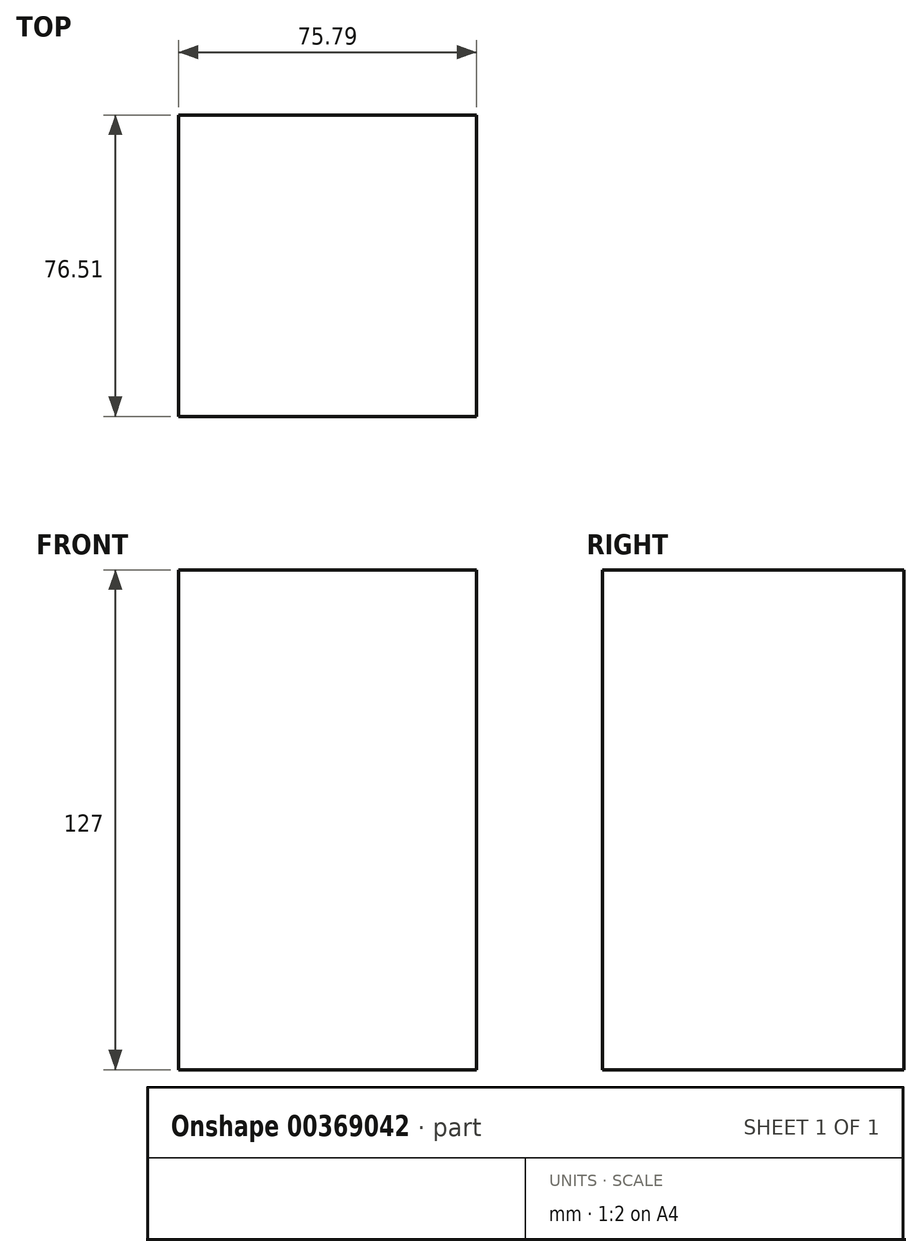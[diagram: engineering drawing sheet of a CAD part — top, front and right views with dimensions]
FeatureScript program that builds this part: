
annotation { "Feature Type Name" : "Feature", "Feature Type Description" : "" }
export const myFeature = defineFeature(function(context is Context, id is Id, definition is map)
    precondition{}
    {
        {
            var Q0;
            Q0=qCreatedBy(makeId("Top.planeOp"),FACE);
            var sketch = newSketch(context, id + "F0", { "sketchPlane" : qUnion([Q0])});
            skLineSegment(sketch, "E0.bottom", {"start": v(0, 0) * mm, "end": v(75.79, 0) * mm});
            skLineSegment(sketch, "E0.top", {"start": v(0, -76.5) * mm, "end": v(75.79, -76.5) * mm});
            skLineSegment(sketch, "E0.left", {"start": v(0, 0) * mm, "end": v(0, -76.5) * mm});
            skLineSegment(sketch, "E0.right", {"start": v(75.79, 0) * mm, "end": v(75.79, -76.5) * mm});
            skSolve(sketch);
        }
        {
            var Q0;
            Q0 = qSketchRegion(id + "F0", true);
            extrude(context, id + "F1", {"entities" : qUnion([Q0]), "depth" : 127 * mm});
        }
        {
            var Q0;
            Q0=makeQuery(id+"F1.opExtrude","CAP_FACE",FACE,{"disambiguationData":[OSD([sQuery(id+"F0.wireOp",EDGE,"E0.bottom"),sQuery(id+"F0.wireOp",EDGE,"E0.top"),sQuery(id+"F0.wireOp",EDGE,"E0.left"),sQuery(id+"F0.wireOp",EDGE,"E0.right")])],"isStart":false});
            var sketch = newSketch(context, id + "F2", { "sketchPlane" : qUnion([Q0])});
            skLineSegment(sketch, "E1.bottom", {"start": v(75.79, -76.5) * mm, "end": v(16.2, -76.5) * mm});
            skLineSegment(sketch, "E1.top", {"start": v(75.79, -15.15) * mm, "end": v(16.2, -15.15) * mm});
            skLineSegment(sketch, "E1.left", {"start": v(75.79, -76.5) * mm, "end": v(75.79, -15.15) * mm});
            skLineSegment(sketch, "E1.right", {"start": v(16.2, -76.5) * mm, "end": v(16.2, -15.15) * mm});
            skSolve(sketch);
        }
        {
            var Q0;
            Q0=makeQuery(id+"F1.opExtrude","SWEPT_FACE",FACE,{"disambiguationData":[OSD([sQuery(id+"F0.wireOp",EDGE,"E0.top")])]});
            var sketch = newSketch(context, id + "F3", { "sketchPlane" : qUnion([Q0])});
            skLineSegment(sketch, "E2", {"start": v(16.43, 127) * mm, "end": v(16.43, 15.63) * mm});
            skLineSegment(sketch, "E3", {"start": v(16.43, 15.63) * mm, "end": v(75.79, 15.63) * mm});
            skSolve(sketch);
        }
        {
            var Q0;
            {var subQ0=sQuery(id+"F3.wireOp",EDGE,"E2");Q0=makeQuery(id+"F3.imprint","IMPRINT",FACE,{"disambiguationData":[TD([[makeQuery(id+"F3.imprint","IMPRINT",EDGE,{"derivedFrom":subQ0}),1.0]])]});}
            extrude(context, id + "F4", {"entities" : qUnion([Q0]), "operationType" : NewBodyOperationType.ADD, "oppositeDirection" : true, "depth" : 37.43 * mm});
        }
    });
